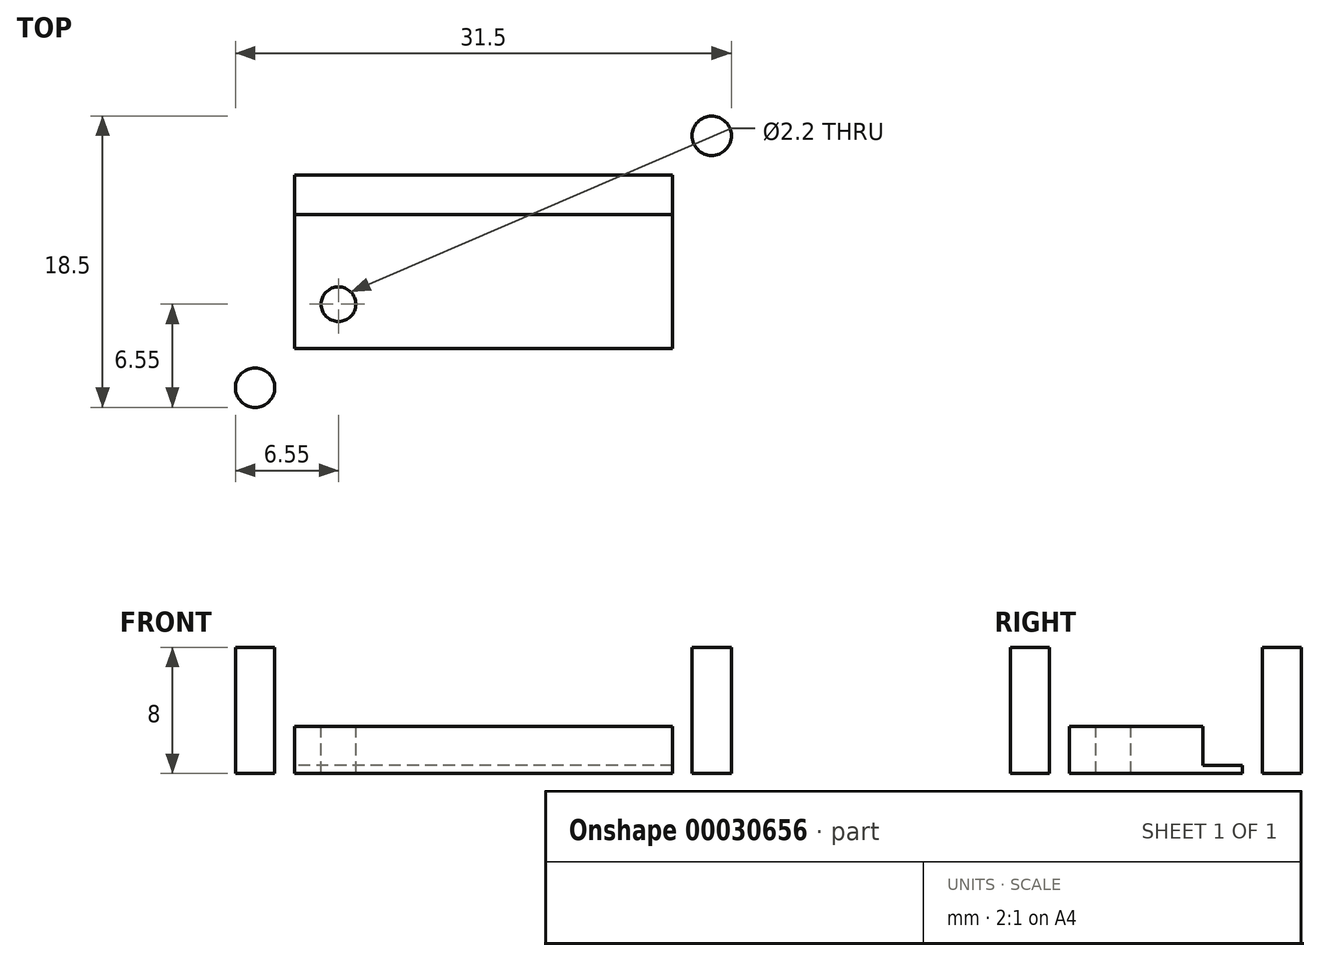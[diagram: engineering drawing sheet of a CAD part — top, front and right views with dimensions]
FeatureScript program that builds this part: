
annotation { "Feature Type Name" : "Feature", "Feature Type Description" : "" }
export const myFeature = defineFeature(function(context is Context, id is Id, definition is map)
    precondition{}
    {
        {
            var Q0;
            Q0=qCreatedBy(makeId("Top.planeOp"),FACE);
            var sketch = newSketch(context, id + "F0", { "sketchPlane" : qUnion([Q0])});
            skLineSegment(sketch, "E0.bottom", {"start": v(0, 0) * mm, "end": v(-34, 0) * mm});
            skLineSegment(sketch, "E0.top", {"start": v(0, 21) * mm, "end": v(-34, 21) * mm});
            skLineSegment(sketch, "E0.left", {"start": v(0, 0) * mm, "end": v(0, 21) * mm});
            skLineSegment(sketch, "E0.right", {"start": v(-34, 0) * mm, "end": v(-34, 21) * mm});
            skLineSegment(sketch, "E1.bottom", {"start": v(-29, 16) * mm, "end": v(-5, 16) * mm});
            skLineSegment(sketch, "E1.top", {"start": v(-29, 5) * mm, "end": v(-5, 5) * mm});
            skLineSegment(sketch, "E1.left", {"start": v(-29, 16) * mm, "end": v(-29, 5) * mm});
            skLineSegment(sketch, "E1.right", {"start": v(-5, 16) * mm, "end": v(-5, 5) * mm});
            skLineSegment(sketch, "E2", {"start": v(-5, 13.5) * mm, "end": v(-29, 13.5) * mm});
            skSolve(sketch);
        }
        {
            var Q0;
            Q0=makeQuery(id+"F0.imprint","IMPRINT",FACE,{"disambiguationData":[TD([[makeQuery(id+"F0.imprint","IMPRINT",EDGE,{"derivedFrom":sQuery(id+"F0.wireOp",EDGE,"E0.bottom")}),-1.0]])]});
            extrude(context, id + "F1", {"entities" : qUnion([Q0]), "depth" : 5 * mm});
        }
        {
            var Q0;
            {var subQ0=sQuery(id+"F0.wireOp",EDGE,"E1.top");Q0=makeQuery(id+"F0.imprint","IMPRINT",FACE,{"disambiguationData":[TD([[makeQuery(id+"F0.imprint","IMPRINT",EDGE,{"derivedFrom":subQ0}),1.0]])]});}
            var Q1;
            Q1=makeQuery(id+"F0.imprint","IMPRINT",FACE,{"disambiguationData":[TD([[makeQuery(id+"F0.imprint","IMPRINT",EDGE,{"derivedFrom":sQuery(id+"F0.wireOp",EDGE,"E0.bottom")}),-1.0]])]});
            var Q2;
            {var subQ0=sQuery(id+"F0.wireOp",EDGE,"E1.bottom");Q2=makeQuery(id+"F0.imprint","IMPRINT",FACE,{"disambiguationData":[TD([[makeQuery(id+"F0.imprint","IMPRINT",EDGE,{"derivedFrom":subQ0}),-1.0]])]});}
            extrude(context, id + "F2", {"entities" : qUnion([Q0, Q1, Q2]), "operationType" : NewBodyOperationType.ADD, "oppositeDirection" : true, "depth" : 3 * mm});
        }
        {
            var Q0;
            {var subQ0=sQuery(id+"F0.wireOp",EDGE,"E1.bottom");Q0=makeQuery(id+"F0.imprint","IMPRINT",FACE,{"disambiguationData":[TD([[makeQuery(id+"F0.imprint","IMPRINT",EDGE,{"derivedFrom":subQ0}),-1.0]])]});}
            extrude(context, id + "F3", {"entities" : qUnion([Q0]), "operationType" : NewBodyOperationType.REMOVE, "oppositeDirection" : true, "depth" : 2.5 * mm});
        }
        {
            var Q0;
            Q0=makeQuery(id+"F2.opExtrude","CAP_FACE",FACE,{"disambiguationData":[OSD([sQuery(id+"F0.wireOp",EDGE,"E0.bottom"),sQuery(id+"F0.wireOp",EDGE,"E0.top"),sQuery(id+"F0.wireOp",EDGE,"E0.left"),sQuery(id+"F0.wireOp",EDGE,"E0.right")])],"isStart":true});
            var sketch = newSketch(context, id + "F4", { "sketchPlane" : qUnion([Q0])});
            skCircle(sketch, "E3", {"center": v(-26.2, 7.8) * mm, "radius": 1.1 * mm});
            skSolve(sketch);
        }
        {
            var Q0;
            Q0=makeQuery(id+"F4.imprint","IMPRINT",FACE,{"disambiguationData":[TD([[makeQuery(id+"F4.imprint","IMPRINT",EDGE,{"derivedFrom":sQuery(id+"F4.wireOp",EDGE,"E3")}),1.0]])]});
            var Q1;
            Q1=makeQuery(id+"F2.opExtrude","CAP_FACE",FACE,{"disambiguationData":[OSD([sQuery(id+"F0.wireOp",EDGE,"E0.bottom"),sQuery(id+"F0.wireOp",EDGE,"E0.top"),sQuery(id+"F0.wireOp",EDGE,"E0.left"),sQuery(id+"F0.wireOp",EDGE,"E0.right")])],"isStart":false});
            extrude(context, id + "F5", {"entities" : qUnion([Q0]), "operationType" : NewBodyOperationType.REMOVE, "endBound" : BoundingType.UP_TO_SURFACE, "oppositeDirection" : true, "endBoundEntityFace" : qUnion([Q1]), "depth" : 25 * mm});
        }
        {
            var Q0;
            Q0=makeQuery(id+"F1.opExtrude","CAP_FACE",FACE,{"disambiguationData":[OSD([sQuery(id+"F0.wireOp",EDGE,"E0.bottom"),sQuery(id+"F0.wireOp",EDGE,"E0.top"),sQuery(id+"F0.wireOp",EDGE,"E0.left"),sQuery(id+"F0.wireOp",EDGE,"E0.right"),sQuery(id+"F0.wireOp",EDGE,"E1.bottom"),sQuery(id+"F0.wireOp",EDGE,"E1.top"),sQuery(id+"F0.wireOp",EDGE,"E1.left"),sQuery(id+"F0.wireOp",EDGE,"E1.right")])],"isStart":false});
            var sketch = newSketch(context, id + "F6", { "sketchPlane" : qUnion([Q0])});
            skLineSegment(sketch, "E4", {"start": v(-34, 21) * mm, "end": v(-29, 16) * mm, "construction": true});
            skCircle(sketch, "E5", {"center": v(-31.5, 18.5) * mm, "radius": 1.25 * mm});
            skLineSegment(sketch, "E6", {"start": v(-17, 21) * mm, "end": v(-17, 0) * mm, "construction": true});
            skCircle(sketch, "E7.MirrorC", {"center": v(-2.5, 18.5) * mm, "radius": 1.25 * mm});
            skLineSegment(sketch, "E8", {"start": v(-34, 10.5) * mm, "end": v(0, 10.5) * mm, "construction": true});
            skCircle(sketch, "E9.MirrorC", {"center": v(-31.5, 2.5) * mm, "radius": 1.25 * mm});
            skCircle(sketch, "E10.MirrorC", {"center": v(-2.5, 2.5) * mm, "radius": 1.25 * mm});
            skSolve(sketch);
        }
        {
            var Q0;
            Q0=makeQuery(id+"F6.imprint","IMPRINT",FACE,{"disambiguationData":[TD([[makeQuery(id+"F6.imprint","IMPRINT",EDGE,{"derivedFrom":sQuery(id+"F6.wireOp",EDGE,"E5")}),1.0]])]});
            var Q1;
            Q1=makeQuery(id+"F6.imprint","IMPRINT",FACE,{"disambiguationData":[TD([[makeQuery(id+"F6.imprint","IMPRINT",EDGE,{"derivedFrom":sQuery(id+"F6.wireOp",EDGE,"E7.MirrorC")}),-1.0]])]});
            var Q2;
            Q2=makeQuery(id+"F6.imprint","IMPRINT",FACE,{"disambiguationData":[TD([[makeQuery(id+"F6.imprint","IMPRINT",EDGE,{"derivedFrom":sQuery(id+"F6.wireOp",EDGE,"E10.MirrorC")}),1.0]])]});
            var Q3;
            Q3=makeQuery(id+"F6.imprint","IMPRINT",FACE,{"disambiguationData":[TD([[makeQuery(id+"F6.imprint","IMPRINT",EDGE,{"derivedFrom":sQuery(id+"F6.wireOp",EDGE,"E9.MirrorC")}),-1.0]])]});
            var Q4;
            Q4=makeQuery(id+"F2.opExtrude","CAP_FACE",FACE,{"disambiguationData":[OSD([sQuery(id+"F0.wireOp",EDGE,"E0.bottom"),sQuery(id+"F0.wireOp",EDGE,"E0.top"),sQuery(id+"F0.wireOp",EDGE,"E0.left"),sQuery(id+"F0.wireOp",EDGE,"E0.right")])],"isStart":false});
            extrude(context, id + "F7", {"entities" : qUnion([Q0, Q1, Q2, Q3]), "operationType" : NewBodyOperationType.REMOVE, "endBound" : BoundingType.UP_TO_SURFACE, "oppositeDirection" : true, "endBoundEntityFace" : qUnion([Q4]), "depth" : 25 * mm});
        }
    });
